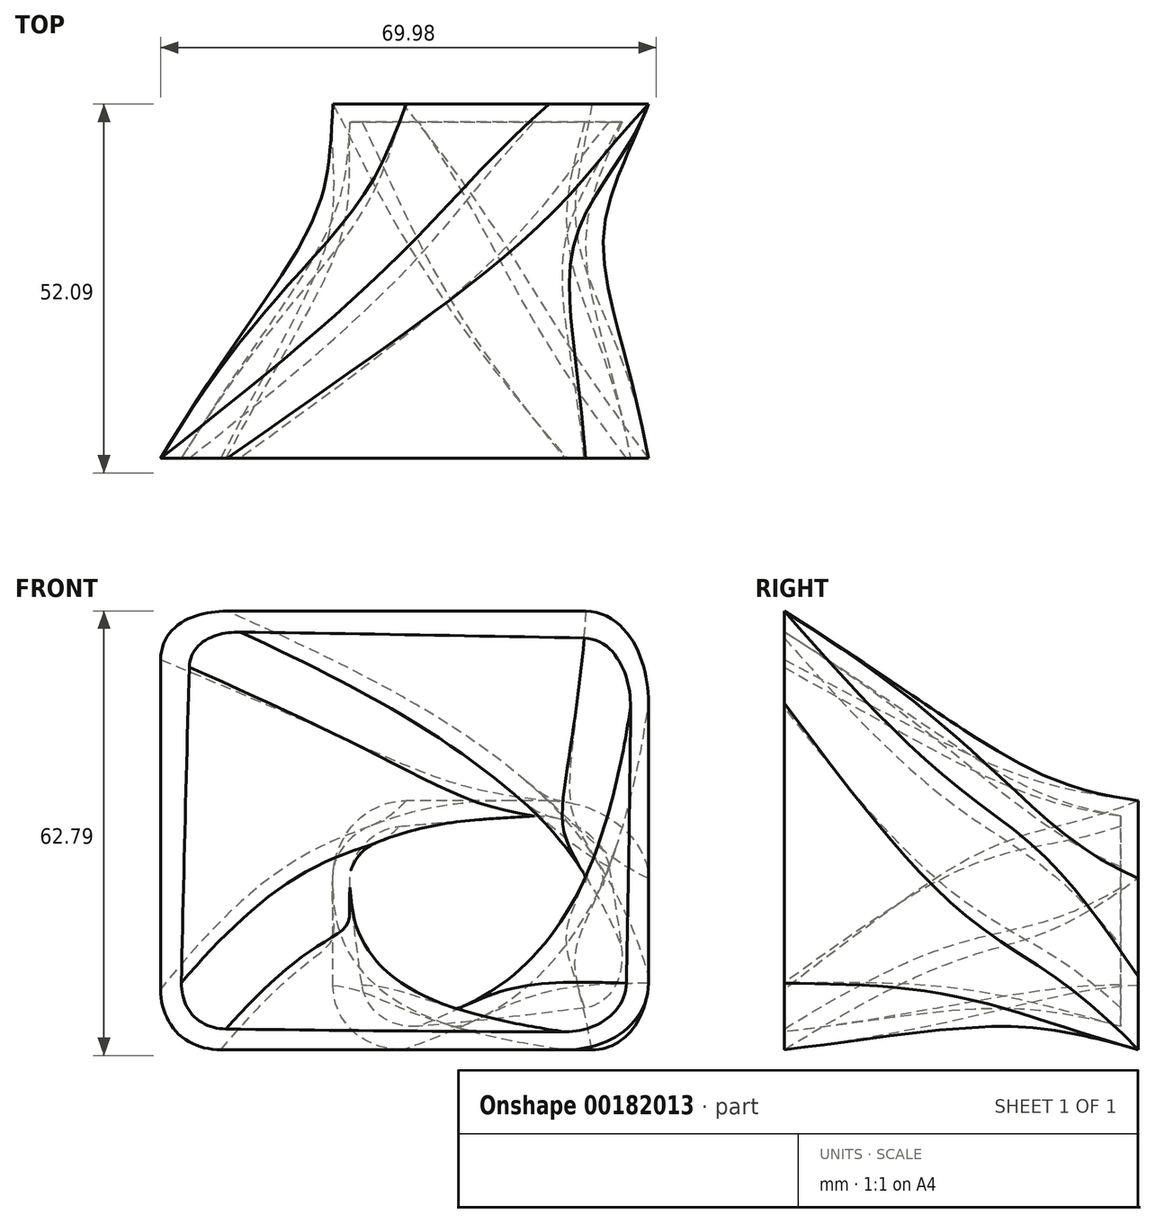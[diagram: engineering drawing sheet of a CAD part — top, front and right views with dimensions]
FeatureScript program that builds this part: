
annotation { "Feature Type Name" : "Feature", "Feature Type Description" : "" }
export const myFeature = defineFeature(function(context is Context, id is Id, definition is map)
    precondition{}
    {
        {
            var Q0;
            Q0=qCreatedBy(makeId("Front.planeOp"),FACE);
            cPlane(context, id + "F0", {"entities" : qUnion([Q0]), "cplaneType" : CPlaneType.OFFSET, "offset" : 50 * mm, "width" : 150 * mm, "height" : 150 * mm});
        }
        {
            var Q0;
            Q0=qCreatedBy(makeId("Front.planeOp"),FACE);
            var sketch = newSketch(context, id + "F1", { "sketchPlane" : qUnion([Q0])});
            skLineSegment(sketch, "E0.bottom", {"start": v(0, 0) * mm, "end": v(-44.55, 0) * mm});
            skLineSegment(sketch, "E0.top", {"start": v(0, 35.17) * mm, "end": v(-44.55, 35.17) * mm});
            skLineSegment(sketch, "E0.left", {"start": v(0, 0) * mm, "end": v(0, 35.17) * mm});
            skLineSegment(sketch, "E0.right", {"start": v(-44.55, 0) * mm, "end": v(-44.55, 35.17) * mm});
            skSolve(sketch);
        }
        {
            var Q0;
            Q0=qCreatedBy(id+"F0.planeOp",FACE);
            var sketch = newSketch(context, id + "F2", { "sketchPlane" : qUnion([Q0])});
            skLineSegment(sketch, "E1.bottom", {"start": v(0, 0) * mm, "end": v(-68.9, 0) * mm});
            skLineSegment(sketch, "E1.top", {"start": v(0, 61.95) * mm, "end": v(-68.9, 61.95) * mm});
            skLineSegment(sketch, "E1.left", {"start": v(0, 0) * mm, "end": v(0, 61.95) * mm});
            skLineSegment(sketch, "E1.right", {"start": v(-68.9, 0) * mm, "end": v(-68.9, 61.95) * mm});
            skSolve(sketch);
        }
        {
            var Q0;
            Q0=qCreatedBy(makeId("Right.planeOp"),FACE);
            var sketch = newSketch(context, id + "F3", { "sketchPlane" : qUnion([Q0])});
            skLineSegment(sketch, "E2", {"start": v(0, 0) * mm, "end": v(-50, 61.95) * mm});
            skSolve(sketch);
        }
        {
            var Q0;
            Q0 = qSketchRegion(id + "F2", true);
            var Q1;
            Q1 = qSketchRegion(id + "F1", true);
            var Q2;
            Q2 = qConstructionFilter(qBodyType(qCreatedBy(id + "F3" ,EDGE), BodyType.WIRE), ConstructionObject.NO);
            loft(context, id + "F4", {"addGuides" : true, "sheetProfilesArray" : [{ "sheetProfileEntities" : qUnion([Q0]) }, { "sheetProfileEntities" : qUnion([Q1]) }], "guidesArray" : [{ "guideEntities" : qUnion([Q2]), "guideDerivativeType" : LoftGuideDerivativeType.DEFAULT, "guideDerivativeMagnitude" : 1 }]});
        }
        {
            var Q0;
            Q0=makeQuery(id+"F4.opLoft","SWEPT_EDGE",EDGE,{"disambiguationData":[OSD([sQuery(id+"F1.wireOp",EDGE,"E0.top"),sQuery(id+"F1.wireOp",EDGE,"E0.left"),sQuery(id+"F2.wireOp",EDGE,"E1.top"),sQuery(id+"F2.wireOp",EDGE,"E1.right")])]});
            var Q1;
            Q1=makeQuery(id+"F4.opLoft","SWEPT_EDGE",EDGE,{"disambiguationData":[OSD([sQuery(id+"F3.wireOp",EDGE,"E2")])]});
            var Q2;
            Q2=makeQuery(id+"F4.opLoft","SWEPT_EDGE",EDGE,{"disambiguationData":[OSD([sQuery(id+"F1.wireOp",EDGE,"E0.bottom"),sQuery(id+"F1.wireOp",EDGE,"E0.right"),sQuery(id+"F2.wireOp",EDGE,"E1.bottom"),sQuery(id+"F2.wireOp",EDGE,"E1.left")])]});
            var Q3;
            Q3=makeQuery(id+"F4.opLoft","SWEPT_EDGE",EDGE,{"disambiguationData":[OSD([sQuery(id+"F1.wireOp",EDGE,"E0.top"),sQuery(id+"F1.wireOp",EDGE,"E0.right"),sQuery(id+"F2.wireOp",EDGE,"E1.bottom"),sQuery(id+"F2.wireOp",EDGE,"E1.right")])]});
            fillet(context, id + "F5", {"entities" : qUnion([Q0, Q1, Q2, Q3]), "radius" : 10 * mm, "tangentPropagation" : true, "allowEdgeOverflow" : false});
        }
        {
            var Q0;
            Q0=makeQuery(id+"F4.opLoft","CAP_FACE",FACE,{"disambiguationData":[OSD([makeQuery(id+"F2.imprint","IMPRINT",FACE,{"disambiguationData":[TD([[makeQuery(id+"F2.imprint","IMPRINT",EDGE,{"derivedFrom":sQuery(id+"F2.wireOp",EDGE,"E1.bottom")}),-1.0]])]})])],"isStart":true});
            shell(context, id + "F6", {"entities" : qUnion([Q0]), "thickness" : 2.5 * mm});
        }
    });
